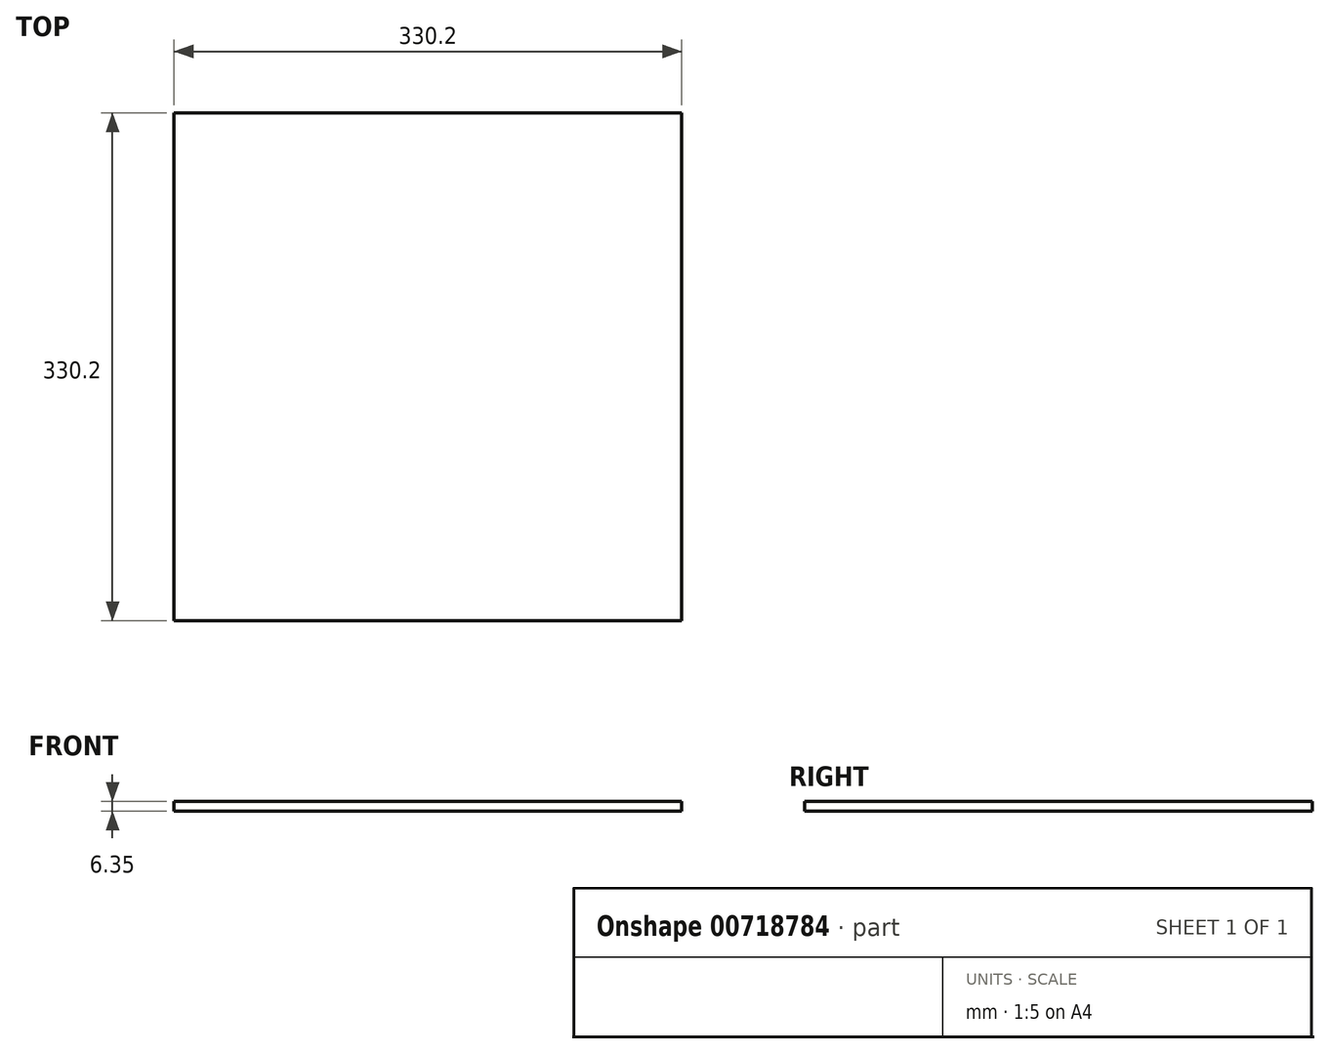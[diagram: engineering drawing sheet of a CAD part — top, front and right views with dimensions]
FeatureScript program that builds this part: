
annotation { "Feature Type Name" : "Feature", "Feature Type Description" : "" }
export const myFeature = defineFeature(function(context is Context, id is Id, definition is map)
    precondition{}
    {
        {
            var Q0;
            Q0=qCreatedBy(makeId("Top.planeOp"),FACE);
            var sketch = newSketch(context, id + "F0", { "sketchPlane" : qUnion([Q0])});
            skLineSegment(sketch, "E0.bottom", {"start": v(-176.23, 191.6) * mm, "end": v(153.97, 191.6) * mm});
            skLineSegment(sketch, "E0.top", {"start": v(-176.23, -138.6) * mm, "end": v(153.97, -138.6) * mm});
            skLineSegment(sketch, "E0.left", {"start": v(-176.23, 191.6) * mm, "end": v(-176.23, -138.6) * mm});
            skLineSegment(sketch, "E0.right", {"start": v(153.97, 191.6) * mm, "end": v(153.97, -138.6) * mm});
            skSolve(sketch);
        }
        {
            var Q0;
            Q0=makeQuery(id+"F0.imprint","IMPRINT",FACE,{"disambiguationData":[TD([[makeQuery(id+"F0.imprint","IMPRINT",EDGE,{"derivedFrom":sQuery(id+"F0.wireOp",EDGE,"E0.bottom")}),-1.0]])]});
            extrude(context, id + "F1", {"entities" : qUnion([Q0]), "depth" : 6.35 * mm, "offsetDistance" : 25.4 * mm});
        }
    });
